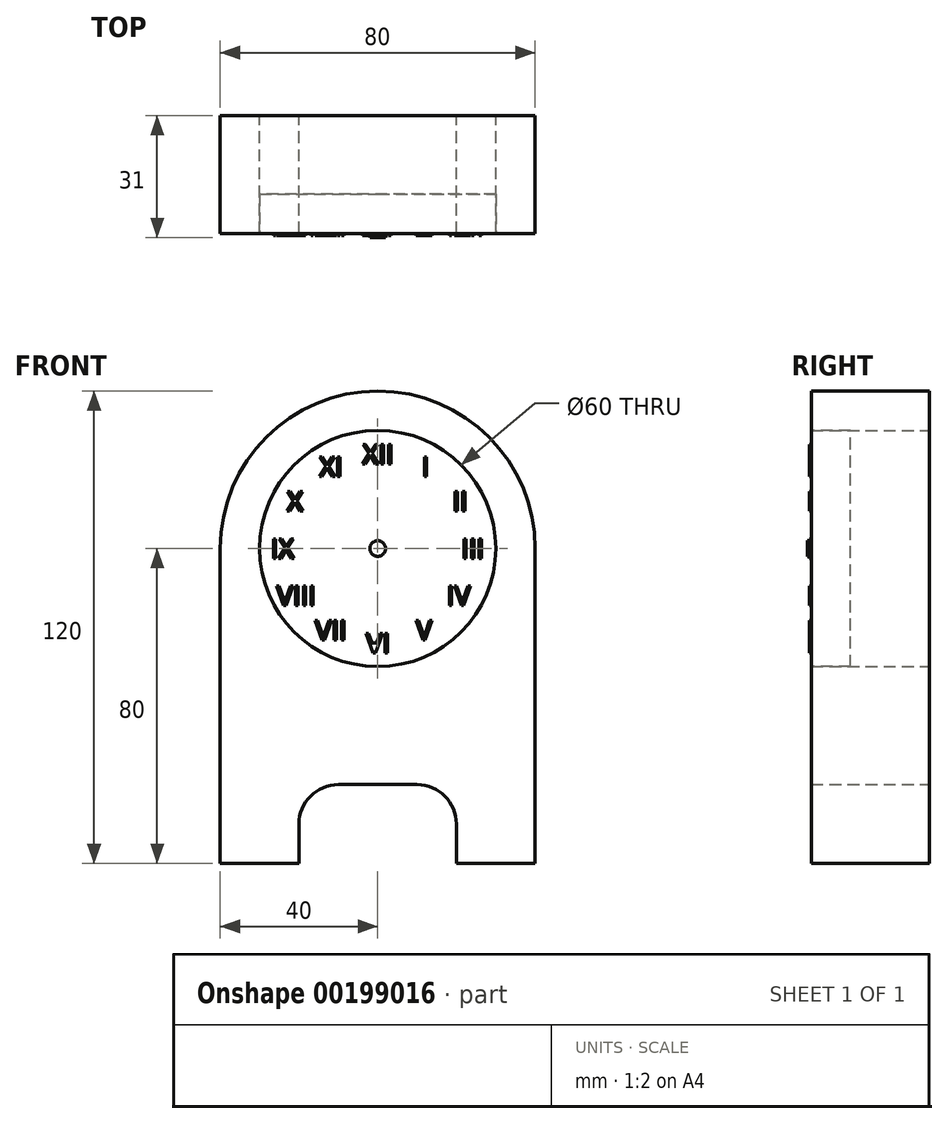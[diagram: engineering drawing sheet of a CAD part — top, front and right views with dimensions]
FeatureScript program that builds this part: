
annotation { "Feature Type Name" : "Feature", "Feature Type Description" : "" }
export const myFeature = defineFeature(function(context is Context, id is Id, definition is map)
    precondition{}
    {
        {
            var Q0;
            Q0=qCreatedBy(makeId("Front.planeOp"),FACE);
            var sketch = newSketch(context, id + "F0", { "sketchPlane" : qUnion([Q0])});
            skCircle(sketch, "E0", {"center": v(0, 0) * mm, "radius": 30 * mm});
            skArc(sketch, "E1", {"start": v(-40, 0) * mm, "mid": v(0, 40) * mm, "end": v(40, 0) * mm});
            skLineSegment(sketch, "E2", {"start": v(-40, 0) * mm, "end": v(-40, -80) * mm});
            skLineSegment(sketch, "E3", {"start": v(-40, -80) * mm, "end": v(-20, -80) * mm});
            skLineSegment(sketch, "E4", {"start": v(40, -80) * mm, "end": v(40, 0) * mm});
            skLineSegment(sketch, "E5", {"start": v(-20, -80) * mm, "end": v(-20, -70) * mm});
            skLineSegment(sketch, "E6", {"start": v(-10, -60) * mm, "end": v(10, -60) * mm});
            skLineSegment(sketch, "E7", {"start": v(20, -70) * mm, "end": v(20, -80) * mm});
            skPoint(sketch, "E8.visualSharp", {"position": v(-20, -60) * mm});
            skArc(sketch, "E8.filletArc", {"start": v(-10, -60) * mm, "mid": v(-17.07, -62.93) * mm, "end": v(-20, -70) * mm});
            skPoint(sketch, "E9.visualSharp", {"position": v(20, -60) * mm});
            skArc(sketch, "E9.filletArc", {"start": v(20, -70) * mm, "mid": v(17.07, -62.93) * mm, "end": v(10, -60) * mm});
            skLineSegment(sketch, "E10.trimOffspring", {"start": v(20, -80) * mm, "end": v(40, -80) * mm});
            skSolve(sketch);
        }
        {
            var Q0;
            Q0=makeQuery(id+"F0.imprint","IMPRINT",FACE,{"disambiguationData":[TD([[makeQuery(id+"F0.imprint","IMPRINT",EDGE,{"derivedFrom":sQuery(id+"F0.wireOp",EDGE,"E0")}),-1.0]])]});
            extrude(context, id + "F1", {"entities" : qUnion([Q0]), "depth" : 30 * mm});
        }
        {
            var Q0;
            Q0=makeQuery(id+"F1.opExtrude","CAP_FACE",FACE,{"disambiguationData":[OSD([sQuery(id+"F0.wireOp",EDGE,"E0"),sQuery(id+"F0.wireOp",EDGE,"E1"),sQuery(id+"F0.wireOp",EDGE,"E2"),sQuery(id+"F0.wireOp",EDGE,"E3"),sQuery(id+"F0.wireOp",EDGE,"E4"),sQuery(id+"F0.wireOp",EDGE,"E5"),sQuery(id+"F0.wireOp",EDGE,"E6"),sQuery(id+"F0.wireOp",EDGE,"E7"),sQuery(id+"F0.wireOp",EDGE,"E8.filletArc"),sQuery(id+"F0.wireOp",EDGE,"E9.filletArc"),sQuery(id+"F0.wireOp",EDGE,"E10.trimOffspring")])],"isStart":false});
            var sketch = newSketch(context, id + "F2", { "sketchPlane" : qUnion([Q0])});
            skCircle(sketch, "E11.0", {"center": v(0, 0) * mm, "radius": 30 * mm});
            skSolve(sketch);
        }
        {
            var Q0;
            Q0=makeQuery(id+"F2.imprint","IMPRINT",FACE,{"disambiguationData":[TD([[makeQuery(id+"F2.imprint","IMPRINT",EDGE,{"derivedFrom":sQuery(id+"F2.wireOp",EDGE,"E11.0")}),1.0]])]});
            extrude(context, id + "F3", {"entities" : qUnion([Q0]), "oppositeDirection" : true, "depth" : 10 * mm});
        }
        {
            var Q0;
            Q0=makeQuery(id+"F3.opExtrude","CAP_FACE",FACE,{"disambiguationData":[OSD([sQuery(id+"F2.wireOp",EDGE,"E11.0")])],"isStart":true});
            var sketch = newSketch(context, id + "F4", { "sketchPlane" : qUnion([Q0])});
            skCircle(sketch, "E12", {"center": v(0, 0) * mm, "radius": 24 * mm, "construction": true});
            skLineSegment(sketch, "E13", {"start": v(20.78, 12) * mm, "end": v(-20.78, -12) * mm, "construction": true});
            skLineSegment(sketch, "E14", {"start": v(12, 20.78) * mm, "end": v(-12, -20.78) * mm, "construction": true});
            skLineSegment(sketch, "E15", {"start": v(-12, 20.78) * mm, "end": v(12, -20.78) * mm, "construction": true});
            skLineSegment(sketch, "E16", {"start": v(-20.78, 12) * mm, "end": v(20.78, -12) * mm, "construction": true});
            skLineSegment(sketch, "E17", {"start": v(-24, 0) * mm, "end": v(24, 0) * mm, "construction": true});
            skLineSegment(sketch, "E18", {"start": v(0, -24) * mm, "end": v(0, 24) * mm, "construction": true});
            skText(sketch, "E19", { "text": "VI", "fontName": "OpenSans-Regular.ttf"});
            skLineSegment(sketch, "E20", {"start": v(-2.92, -24) * mm, "end": v(2.92, -24) * mm});
            skText(sketch, "E21", { "text": "XII", "fontName": "OpenSans-Regular.ttf"});
            skLineSegment(sketch, "E22", {"start": v(-3.83, 24) * mm, "end": v(3.83, 24) * mm, "construction": true});
            skText(sketch, "E23", { "text": "I", "fontName": "OpenSans-Regular.ttf"});
            skLineSegment(sketch, "E24", {"start": v(11.15, 20.78) * mm, "end": v(12.85, 20.78) * mm, "construction": true});
            skText(sketch, "E25", { "text": "II", "fontName": "OpenSans-Regular.ttf"});
            skLineSegment(sketch, "E26", {"start": v(18.96, 12) * mm, "end": v(22.6, 12) * mm, "construction": true});
            skText(sketch, "E27", { "text": "III", "fontName": "OpenSans-Regular.ttf"});
            skLineSegment(sketch, "E28", {"start": v(21.21, 0) * mm, "end": v(26.79, 0) * mm, "construction": true});
            skText(sketch, "E29", { "text": "IV", "fontName": "OpenSans-Regular.ttf"});
            skLineSegment(sketch, "E30", {"start": v(17.53, -12) * mm, "end": v(24.04, -12) * mm, "construction": true});
            skText(sketch, "E31", { "text": "V", "fontName": "OpenSans-Regular.ttf"});
            skLineSegment(sketch, "E32", {"start": v(9.7, -20.78) * mm, "end": v(14.3, -20.78) * mm, "construction": true});
            skText(sketch, "E33", { "text": "VII", "fontName": "OpenSans-Regular.ttf"});
            skLineSegment(sketch, "E34", {"start": v(-15.89, -20.78) * mm, "end": v(-8.11, -20.78) * mm, "construction": true});
            skText(sketch, "E35", { "text": "VIII", "fontName": "OpenSans-Regular.ttf"});
            skLineSegment(sketch, "E36", {"start": v(-25.64, -12) * mm, "end": v(-15.93, -12) * mm, "construction": true});
            skText(sketch, "E37", { "text": "IX", "fontName": "OpenSans-Regular.ttf"});
            skLineSegment(sketch, "E38", {"start": v(-27.18, 0) * mm, "end": v(-20.82, 0) * mm, "construction": true});
            skText(sketch, "E39", { "text": "X", "fontName": "OpenSans-Regular.ttf"});
            skLineSegment(sketch, "E40", {"start": v(-23, 12) * mm, "end": v(-18.57, 12) * mm, "construction": true});
            skText(sketch, "E41", { "text": "XI", "fontName": "OpenSans-Regular.ttf"});
            skLineSegment(sketch, "E42", {"start": v(-14.86, 20.78) * mm, "end": v(-9.14, 20.78) * mm, "construction": true});
            const initialGuessF4  = {"E19": [-0.00292, -0.0265, 1, 0, 0.005], "E21": [-0.00383, 0.0215, 1, 0, 0.005], "E23": [0.01115, 0.01828, 1, 0, 0.005], "E25": [0.01896, 0.0095, 1, 0, 0.005], "E27": [0.02121, -0.0025, 1, 0, 0.005], "E29": [0.01753, -0.0145, 1, 0, 0.005], "E31": [0.0097, -0.02328, 1, 0, 0.005], "E33": [-0.01589, -0.02328, 1, 0, 0.005], "E35": [-0.02564, -0.0145, 1, 0, 0.005], "E37": [-0.02718, -0.0025, 1, 0, 0.005], "E39": [-0.023, 0.0095, 1, 0, 0.005], "E41": [-0.01486, 0.01828, 1, 0, 0.005]};
            skSetInitialGuess(sketch, initialGuessF4);
            skSolve(sketch);
        }
        {
            var Q0;
            Q0 = qSketchRegion(id + "F4", true);
            extrude(context, id + "F5", {"entities" : qUnion([Q0]), "operationType" : NewBodyOperationType.ADD, "depth" : 0.5 * mm});
        }
        {
            var Q0;
            Q0=makeQuery(id+"F3.opExtrude","CAP_FACE",FACE,{"disambiguationData":[OSD([sQuery(id+"F2.wireOp",EDGE,"E11.0")])],"isStart":true});
            var sketch = newSketch(context, id + "F6", { "sketchPlane" : qUnion([Q0])});
            skCircle(sketch, "E43", {"center": v(0, 0) * mm, "radius": 2 * mm});
            skSolve(sketch);
        }
        {
            var Q0;
            Q0=makeQuery(id+"F6.imprint","IMPRINT",FACE,{"disambiguationData":[TD([[makeQuery(id+"F6.imprint","IMPRINT",EDGE,{"derivedFrom":sQuery(id+"F6.wireOp",EDGE,"E43")}),1.0]])]});
            extrude(context, id + "F7", {"entities" : qUnion([Q0]), "depth" : 1 * mm});
        }
    });
